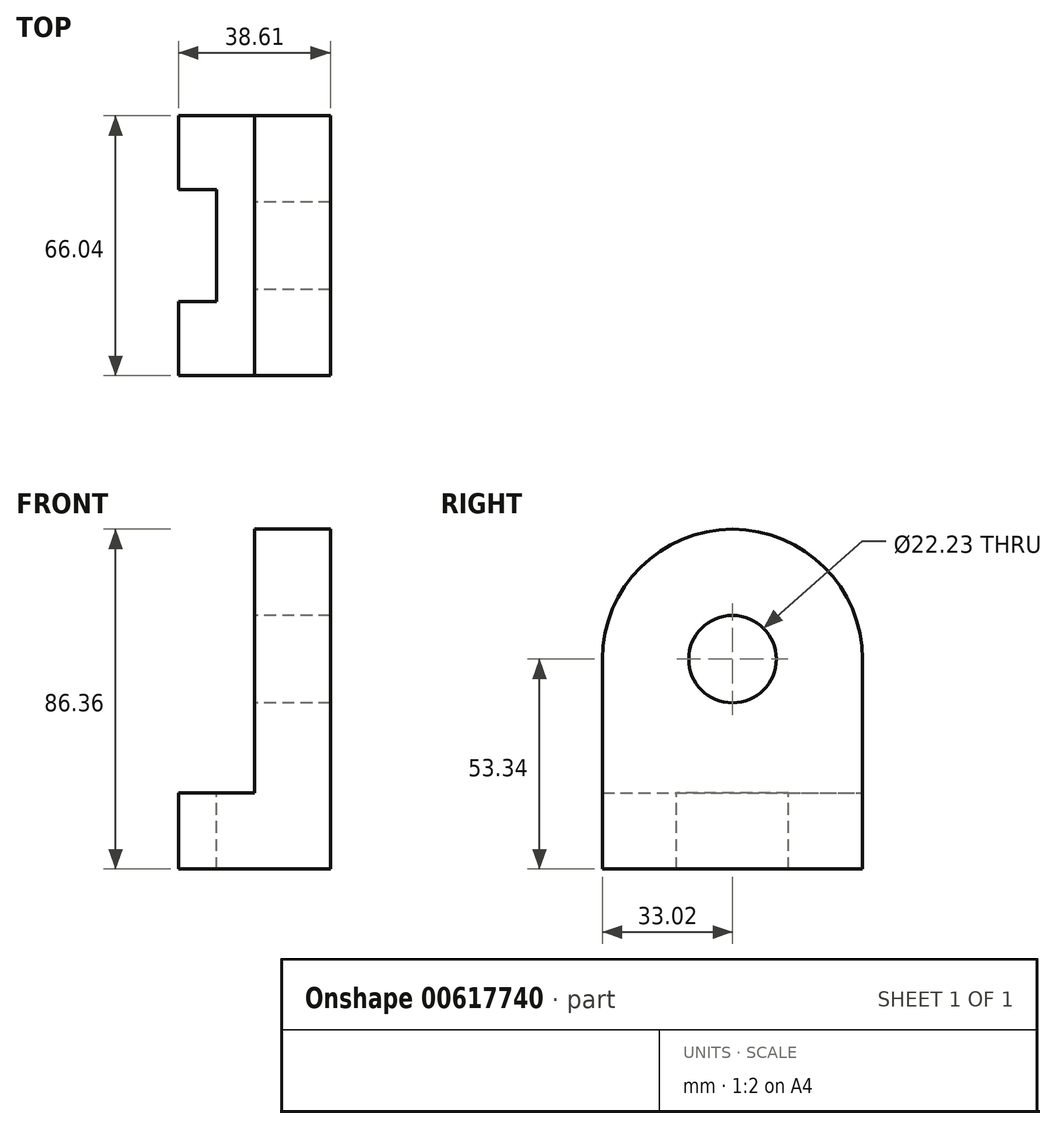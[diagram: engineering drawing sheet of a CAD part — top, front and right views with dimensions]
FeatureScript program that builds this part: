
annotation { "Feature Type Name" : "Feature", "Feature Type Description" : "" }
export const myFeature = defineFeature(function(context is Context, id is Id, definition is map)
    precondition{}
    {
        {
            var Q0;
            Q0=qCreatedBy(makeId("Front.planeOp"),FACE);
            var sketch = newSketch(context, id + "F0", { "sketchPlane" : qUnion([Q0])});
            skLineSegment(sketch, "E0", {"start": v(0, 0) * mm, "end": v(38.6, 0) * mm});
            skLineSegment(sketch, "E1", {"start": v(38.6, 0) * mm, "end": v(38.6, 86.36) * mm});
            skLineSegment(sketch, "E2", {"start": v(38.6, 86.36) * mm, "end": v(19.3, 86.36) * mm});
            skLineSegment(sketch, "E3", {"start": v(19.3, 86.36) * mm, "end": v(19.3, 19.3) * mm});
            skLineSegment(sketch, "E4", {"start": v(19.3, 19.3) * mm, "end": v(0, 19.3) * mm});
            skLineSegment(sketch, "E5", {"start": v(0, 19.3) * mm, "end": v(0, 0) * mm});
            skSolve(sketch);
        }
        {
            var Q0;
            Q0 = qSketchRegion(id + "F0", true);
            extrude(context, id + "F1", {"entities" : qUnion([Q0]), "depth" : 66.04 * mm, "offsetDistance" : 25.4 * mm});
        }
        {
            var Q0;
            Q0=makeQuery(id+"F1.opExtrude","CAP_EDGE",EDGE,{"disambiguationData":[OSD([sQuery(id+"F0.wireOp",EDGE,"E2")])],"isStart":false});
            var Q1;
            Q1=makeQuery(id+"F1.opExtrude","CAP_EDGE",EDGE,{"disambiguationData":[OSD([sQuery(id+"F0.wireOp",EDGE,"E2")])],"isStart":true});
            fillet(context, id + "F2", {"entities" : qUnion([Q0, Q1]), "radius" : 33.02 * mm, "tangentPropagation" : true, "allowEdgeOverflow" : false});
        }
        {
            var Q0;
            Q0=makeQuery(id+"F1.opExtrude","SWEPT_FACE",FACE,{"disambiguationData":[OSD([sQuery(id+"F0.wireOp",EDGE,"E3")])]});
            var sketch = newSketch(context, id + "F3", { "sketchPlane" : qUnion([Q0])});
            skCircle(sketch, "E6", {"center": v(33.02, 53.34) * mm, "radius": 11.11 * mm});
            skSolve(sketch);
        }
        {
            var Q0;
            Q0=makeQuery(id+"F1.opExtrude","SWEPT_FACE",FACE,{"disambiguationData":[OSD([sQuery(id+"F0.wireOp",EDGE,"E4")])]});
            var sketch = newSketch(context, id + "F4", { "sketchPlane" : qUnion([Q0])});
            skPoint(sketch, "E7.oppositeSnap0", {"position": v(9.65, 0) * mm});
            skLineSegment(sketch, "E7.bottom", {"start": v(0, -18.8) * mm, "end": v(9.65, -18.8) * mm});
            skLineSegment(sketch, "E7.top", {"start": v(0, -47.24) * mm, "end": v(9.65, -47.24) * mm});
            skLineSegment(sketch, "E7.left", {"start": v(0, -18.8) * mm, "end": v(0, -47.24) * mm});
            skLineSegment(sketch, "E7.right", {"start": v(9.65, -18.8) * mm, "end": v(9.65, -47.24) * mm});
            skPoint(sketch, "E8", {"position": v(0, -33.02) * mm});
            skSolve(sketch);
        }
        {
            var Q0;
            Q0=makeQuery(id+"F4.imprint","IMPRINT",FACE,{"disambiguationData":[TD([[makeQuery(id+"F4.imprint","IMPRINT",EDGE,{"derivedFrom":sQuery(id+"F4.wireOp",EDGE,"E7.bottom")}),-1.0]])]});
            extrude(context, id + "F5", {"entities" : qUnion([Q0]), "operationType" : NewBodyOperationType.REMOVE, "oppositeDirection" : true, "depth" : 30.23 * mm, "offsetDistance" : 25.4 * mm});
        }
        {
            var Q0;
            Q0=makeQuery(id+"F3.imprint","IMPRINT",FACE,{"disambiguationData":[TD([[makeQuery(id+"F3.imprint","IMPRINT",EDGE,{"derivedFrom":sQuery(id+"F3.wireOp",EDGE,"E6")}),1.0]])]});
            extrude(context, id + "F6", {"entities" : qUnion([Q0]), "operationType" : NewBodyOperationType.REMOVE, "oppositeDirection" : true, "depth" : 63.25 * mm, "offsetDistance" : 25.4 * mm});
        }
    });
